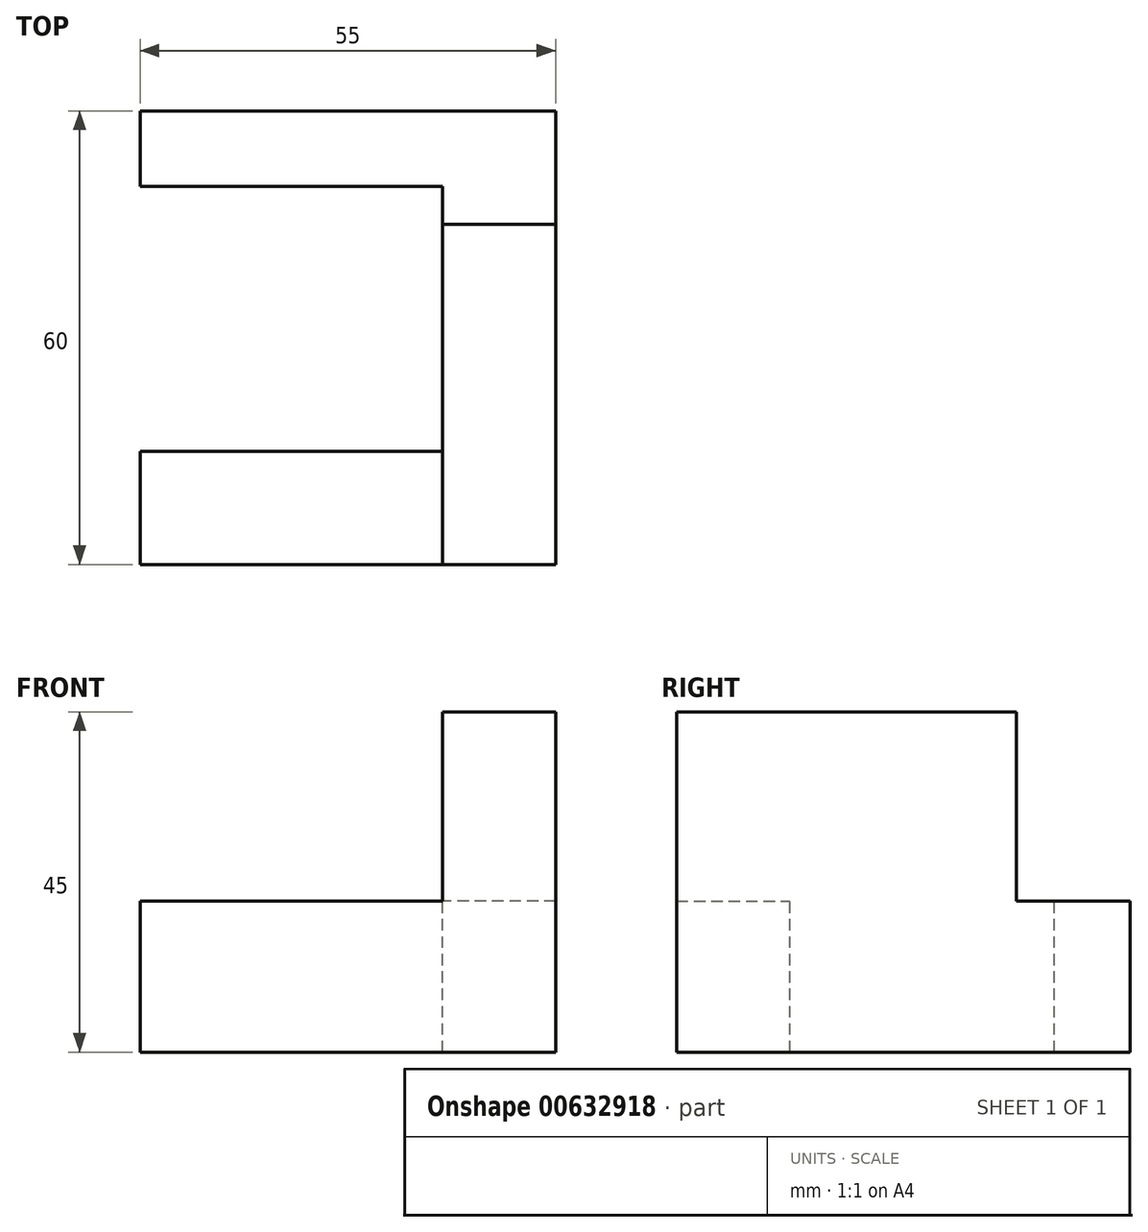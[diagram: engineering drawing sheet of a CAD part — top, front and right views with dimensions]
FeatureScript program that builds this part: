
annotation { "Feature Type Name" : "Feature", "Feature Type Description" : "" }
export const myFeature = defineFeature(function(context is Context, id is Id, definition is map)
    precondition{}
    {
        {
            var Q0;
            Q0=qCreatedBy(makeId("Top.planeOp"),FACE);
            var sketch = newSketch(context, id + "F0", { "sketchPlane" : qUnion([Q0])});
            skLineSegment(sketch, "E0.bottom", {"start": v(27.5, 30) * mm, "end": v(-27.5, 30) * mm});
            skLineSegment(sketch, "E0.top", {"start": v(27.5, -30) * mm, "end": v(-27.5, -30) * mm});
            skLineSegment(sketch, "E0.left", {"start": v(27.5, 30) * mm, "end": v(27.5, -30) * mm});
            skLineSegment(sketch, "E0.right", {"start": v(-27.5, 30) * mm, "end": v(-27.5, -30) * mm});
            skPoint(sketch, "E0.middle", {"position": v(0, 0) * mm});
            skSolve(sketch);
        }
        {
            var Q0;
            Q0 = qSketchRegion(id + "F0", true);
            extrude(context, id + "F1", {"entities" : qUnion([Q0]), "depth" : 45 * mm, "offsetDistance" : 25 * mm});
        }
        {
            var Q0;
            Q0=makeQuery(id+"F1.opExtrude","SWEPT_FACE",FACE,{"disambiguationData":[OSD([sQuery(id+"F0.wireOp",EDGE,"E0.bottom")])]});
            var sketch = newSketch(context, id + "F2", { "sketchPlane" : qUnion([Q0])});
            skLineSegment(sketch, "E1", {"start": v(-27.5, 0) * mm, "end": v(-27.5, 20) * mm});
            skLineSegment(sketch, "E2", {"start": v(-27.5, 20) * mm, "end": v(27.5, 20) * mm});
            skLineSegment(sketch, "E3", {"start": v(27.5, 20) * mm, "end": v(27.5, 0) * mm});
            skLineSegment(sketch, "E4", {"start": v(27.5, 0) * mm, "end": v(-27.5, 0) * mm});
            skSolve(sketch);
        }
        {
            var Q0;
            {var subQ0=sQuery(id+"F2.wireOp",EDGE,"E2");Q0=makeQuery(id+"F2.imprint","IMPRINT",FACE,{"disambiguationData":[TD([[makeQuery(id+"F2.imprint","IMPRINT",EDGE,{"derivedFrom":subQ0}),1.0]])]});}
            extrude(context, id + "F3", {"entities" : qUnion([Q0]), "operationType" : NewBodyOperationType.REMOVE, "oppositeDirection" : true, "depth" : 15 * mm, "offsetDistance" : 25 * mm});
        }
        {
            var Q0;
            Q0=makeQuery(id+"F3.boolean.opBoolean","COPY",FACE,{"derivedFrom":makeQuery(id+"F3.opExtrude","SWEPT_FACE",FACE,{"disambiguationData":[OSD([sQuery(id+"F2.wireOp",EDGE,"E2")])]})});
            var sketch = newSketch(context, id + "F4", { "sketchPlane" : qUnion([Q0])});
            skLineSegment(sketch, "E5", {"start": v(12.5, 20) * mm, "end": v(12.5, 15) * mm});
            skLineSegment(sketch, "E6", {"start": v(12.5, 15) * mm, "end": v(27.5, 15) * mm});
            skLineSegment(sketch, "E7", {"start": v(27.5, 15) * mm, "end": v(27.5, 30) * mm});
            skLineSegment(sketch, "E8", {"start": v(-27.5, 30) * mm, "end": v(-27.5, 20) * mm});
            skLineSegment(sketch, "E9", {"start": v(-27.5, 20) * mm, "end": v(12.5, 20) * mm});
            skPoint(sketch, "E10.orphan", {"position": v(12.5, 22.5) * mm});
            skSolve(sketch);
        }
        {
            var Q0;
            {var subQ0=sQuery(id+"F4.wireOp",EDGE,"E5");Q0=makeQuery(id+"F4.imprint","IMPRINT",FACE,{"disambiguationData":[TD([[makeQuery(id+"F4.imprint","IMPRINT",EDGE,{"derivedFrom":subQ0}),-1.0]])]});}
            extrude(context, id + "F5", {"entities" : qUnion([Q0]), "operationType" : NewBodyOperationType.REMOVE, "endBound" : BoundingType.THROUGH_ALL, "oppositeDirection" : true, "depth" : 25 * mm, "offsetDistance" : 25 * mm});
        }
        {
            var Q0;
            {var subQ0=sQuery(id+"F2.wireOp",EDGE,"E2");Q0=makeQuery(id+"F5.boolean.opBoolean","MERGE",FACE,{"derivedFrom":[makeQuery(id+"F3.boolean.opBoolean","COPY",FACE,{"derivedFrom":makeQuery(id+"F3.opExtrude","CAP_FACE",FACE,{"disambiguationData":[OSD([sQuery(id+"F0.wireOp",EDGE,"E0.bottom"),sQuery(id+"F0.wireOp",EDGE,"E0.left"),sQuery(id+"F0.wireOp",EDGE,"E0.right"),subQ0])],"isStart":false})}),makeQuery(id+"F5.opExtrude","SWEPT_FACE",FACE,{"disambiguationData":[OSD([subQ0])]})]});}
            var sketch = newSketch(context, id + "F6", { "sketchPlane" : qUnion([Q0])});
            skLineSegment(sketch, "E11", {"start": v(-12.5, 20) * mm, "end": v(-12.5, 45) * mm});
            skLineSegment(sketch, "E12", {"start": v(-12.5, 45) * mm, "end": v(-27.5, 45) * mm});
            skLineSegment(sketch, "E13", {"start": v(-27.5, 45) * mm, "end": v(-27.5, 20) * mm});
            skLineSegment(sketch, "E14", {"start": v(-27.5, 20) * mm, "end": v(-12.5, 20) * mm});
            skSolve(sketch);
        }
        {
            var Q0;
            {var subQ5=sQuery(id+"F6.wireOp",EDGE,"E11");Q0=makeQuery(id+"F6.imprint","IMPRINT",FACE,{"disambiguationData":[TD([[makeQuery(id+"F6.imprint","IMPRINT",EDGE,{"derivedFrom":subQ5}),-1.0]])]});}
            extrude(context, id + "F7", {"entities" : qUnion([Q0]), "operationType" : NewBodyOperationType.REMOVE, "endBound" : BoundingType.THROUGH_ALL, "oppositeDirection" : true, "depth" : 25 * mm, "offsetDistance" : 25 * mm});
        }
        {
            var Q0;
            {var subQ0=sQuery(id+"F4.wireOp",EDGE,"E5");Q0=makeQuery(id+"F7.boolean.opBoolean","MERGE",FACE,{"derivedFrom":[makeQuery(id+"F5.boolean.opBoolean","COPY",FACE,{"derivedFrom":makeQuery(id+"F5.opExtrude","SWEPT_FACE",FACE,{"disambiguationData":[OSD([subQ0])]})}),makeQuery(id+"F7.opExtrude","SWEPT_FACE",FACE,{"disambiguationData":[OSD([sQuery(id+"F2.wireOp",EDGE,"E2"),subQ0,sQuery(id+"F4.wireOp",EDGE,"E6"),sQuery(id+"F6.wireOp",EDGE,"E11")])]})]});}
            var sketch = newSketch(context, id + "F8", { "sketchPlane" : qUnion([Q0])});
            skLineSegment(sketch, "E15.bottom", {"start": v(30, 0) * mm, "end": v(15, 0) * mm});
            skLineSegment(sketch, "E15.top", {"start": v(30, 20) * mm, "end": v(15, 20) * mm});
            skLineSegment(sketch, "E15.left", {"start": v(30, 0) * mm, "end": v(30, 20) * mm});
            skLineSegment(sketch, "E15.right", {"start": v(15, 0) * mm, "end": v(15, 20) * mm});
            skSolve(sketch);
        }
        {
            var Q0;
            Q0 = qSketchRegion(id + "F8", true);
            extrude(context, id + "F9", {"entities" : qUnion([Q0]), "operationType" : NewBodyOperationType.ADD, "depth" : 40 * mm, "offsetDistance" : 25 * mm});
        }
    });
